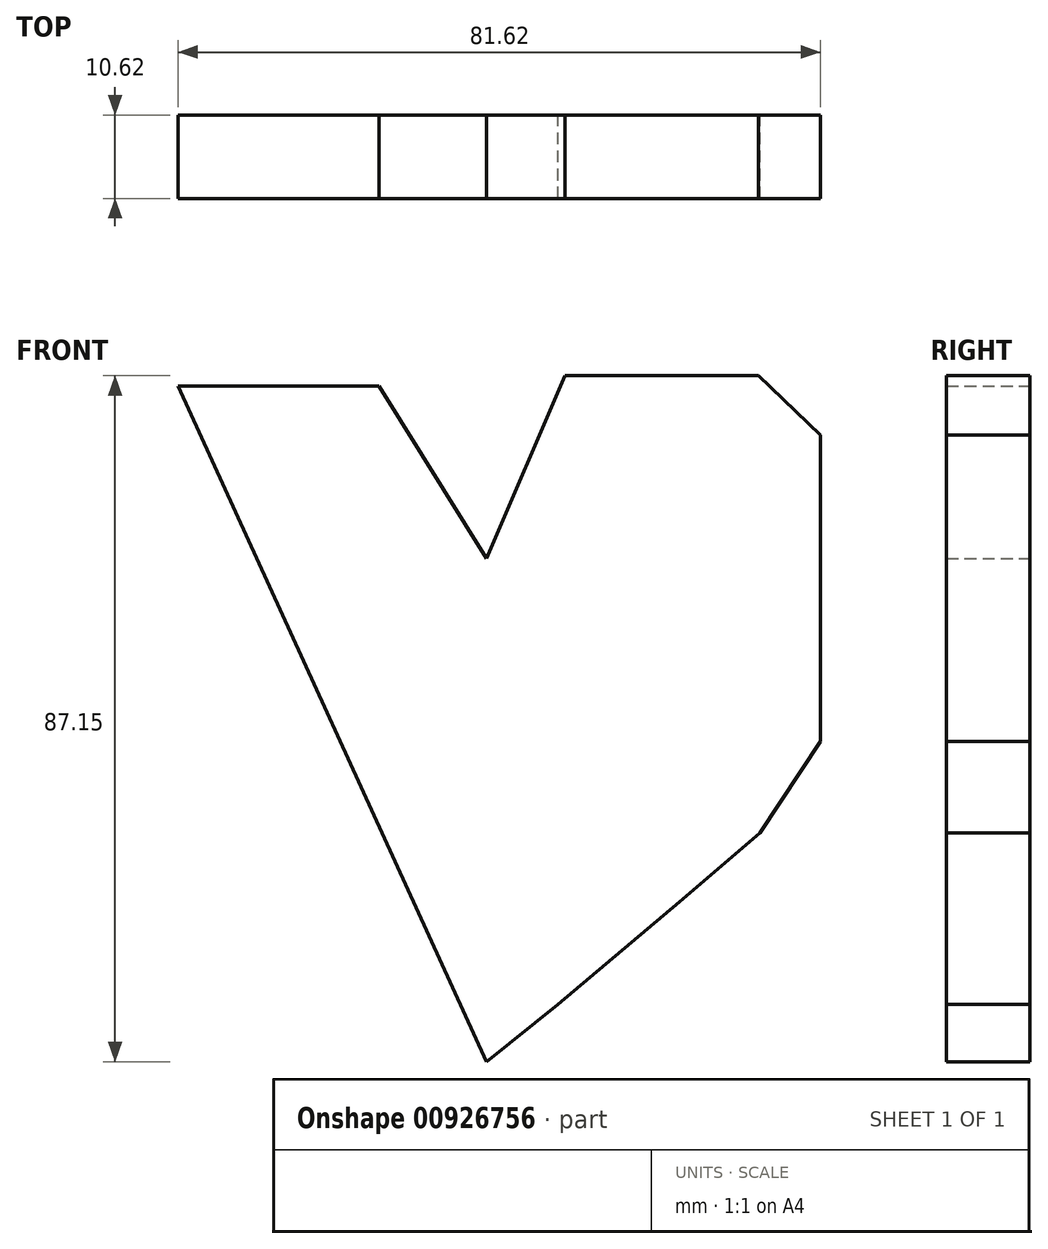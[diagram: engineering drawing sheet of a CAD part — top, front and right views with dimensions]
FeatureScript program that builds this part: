
annotation { "Feature Type Name" : "Feature", "Feature Type Description" : "" }
export const myFeature = defineFeature(function(context is Context, id is Id, definition is map)
    precondition{}
    {
        {
            var Q0;
            Q0=qCreatedBy(makeId("Front.planeOp"),FACE);
            var sketch = newSketch(context, id + "F0", { "sketchPlane" : qUnion([Q0])});
            skLineSegment(sketch, "E0", {"start": v(0, -47.67) * mm, "end": v(9.06, -40.37) * mm});
            skLineSegment(sketch, "E1", {"start": v(9.06, -40.37) * mm, "end": v(24.52, -27.36) * mm});
            skLineSegment(sketch, "E2", {"start": v(24.52, -27.36) * mm, "end": v(34.76, -18.62) * mm});
            skLineSegment(sketch, "E3", {"start": v(34.76, -18.62) * mm, "end": v(42.44, -6.99) * mm});
            skLineSegment(sketch, "E4", {"start": v(42.44, -6.99) * mm, "end": v(42.44, 22.7) * mm});
            skLineSegment(sketch, "E5", {"start": v(42.44, 22.7) * mm, "end": v(42.44, 31.94) * mm});
            skLineSegment(sketch, "E6", {"start": v(42.44, 31.94) * mm, "end": v(34.57, 39.48) * mm});
            skLineSegment(sketch, "E7", {"start": v(34.57, 39.48) * mm, "end": v(9.98, 39.48) * mm});
            skLineSegment(sketch, "E8", {"start": v(9.98, 39.48) * mm, "end": v(0, 16.27) * mm});
            skLineSegment(sketch, "E9", {"start": v(0, 16.27) * mm, "end": v(-13.62, 38.17) * mm});
            skLineSegment(sketch, "E10", {"start": v(-13.62, 38.17) * mm, "end": v(-39.18, 38.17) * mm});
            skLineSegment(sketch, "E11", {"start": v(-39.18, 38.17) * mm, "end": v(0, -47.67) * mm});
            skLineSegment(sketch, "E12", {"start": v(-8.97, -28.02) * mm, "end": v(-13.26, -18.62) * mm});
            skSolve(sketch);
        }
        {
            var Q0;
            Q0 = qSketchRegion(id + "F0", true);
            extrude(context, id + "F1", {"entities" : qUnion([Q0]), "depth" : 10.62 * mm, "offsetDistance" : 25.4 * mm});
        }
    });
